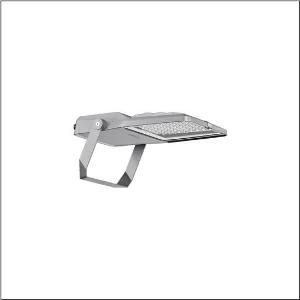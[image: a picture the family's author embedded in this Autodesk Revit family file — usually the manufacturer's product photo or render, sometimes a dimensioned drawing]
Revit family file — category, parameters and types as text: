
# Revit family: floodlight_fl_21_iq_mini___pl64_5xa7772d5e1a_506a
name_source: partatom
category: Lighting Fixtures
units: mm (PartAtom-declared; Revit-internal decimal feet)

## family parameters
Cut with Voids When Loaded = No
Host = Face
Light Source = No
Part Type = Normal
Room Calculation Point = No
Round Connector Dimension = Use Diameter
Shared = No

## types (1)
- --- (1 x LED, 16070 lm, 143 W, 4000K)
    Apparent Load = 143 VA
    CIE Flux Codes = 28 80 98 100 100
    Color Rendering = 80
    Color Temperature = 4000K
    Default Elevation = 1800 mm
    Description = Floodlight FL 21 iQ mini, floodlight, primary light control with lens, of PMMA, primary optical cover: protective disc, of toughened safety glass, transparent, light distribution: PL64, light emission: direct distribution, installation type: surface-mounted, LED, High Power LED, rated luminous flux: 16.070lm, luminous efficacy: 112lm/W, light colour: 840, colour temperature: 4000K, control: Street-Remote, Auto-Match, Temp-Guard, Night-Set, Smart-Wire, Desk-Remote (wireless, voltage-free reading and setting of iQ features in the workshop via application-optimized NFC function/RFID function), optimised constant luminous flux control (CLO 2.0), with terminal, 6-pole, mains connection: 220..240V, AC, 50/60Hz, start of lifetime: 143W, end of service life: 152W, reduction: 61W, luminaire housing, of diecast aluminium, powder-coated, Siteco® metallic grey (DB 702S), corrosivity category C5 mid according to DIN EN ISO 12944, sealing non-destructively replaceable, mounting bracket, of steel, galvanised, powder-coated, Siteco® metallic grey (DB 702S), protection rating (complete): IP66, insulation class (complete): insulation class II (safety insulation), certification: CE, ENEC, VDE, protection symbol: D, impact resistance: IK08, permissible operating ambient temperature: -40..+40°C, permissible operating ambient temperature for outdoor applications: -40..+50°C, standard: DIN EN 12944, LABS conformity tested according to VDMA 24364:2018-05, packaging unit: 1 piece

Light Distribution: PL64
    Height = 70 mm
    Lamp = 1 x LED
    Lamp Light Flux = 16070 lm
    Lamp Power = 143 W
    Lamp count = 1
    Length = 485 mm
    Luminous efficacy = 112 lm/W
    Manufacturer = Siteco
    ModVariant = No
    Model = 5XA7772D5E1A
    Number of Poles = 1
    OnlyDefault = Yes
    Power Factor = 1
    Product Name = Floodlight FL 21 iQ mini | PL64
    Product group = floodlight | pylon annexe
    ProductGroupID = 6200
    Protection Class = Protection class II
    Protection Degree = IP 66
    RLX_Detail_Level = 1
    RLX_Emergency_Light_Flux = 0 lm
    RLX_Emergency_Type = 0
    RLX_Emergency_Type_DB = No
    RlxData = <blob elided: 96545 chars, md5=ee79a65b>
    Socket = socket
    Standby Power = 0 W
    System Light Flux = 16070 lm
    System Power = 143 W
    Type Comments = factory setting: luminous flux: 100 % | dim-lin: 254 | 730 mA
    Type Image = l_1006845.jpg
    URL = http://relux.com
    VarID = @adj_097911
    Voltage = 0 V
    Weight = 0.00 kg
    Width = 337 mm

## geometry (parser evidence)
native form markers: Blend x4, Sweep x12
no freeform markers — native parametric forms only
